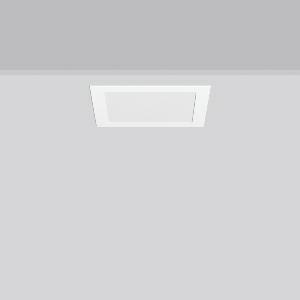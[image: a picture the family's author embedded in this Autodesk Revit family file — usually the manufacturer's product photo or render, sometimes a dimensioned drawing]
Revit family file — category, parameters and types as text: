
# Revit family: toledo_flat_square_e_901487_002_7142
name_source: partatom
category: Lighting Fixtures
units: mm (PartAtom-declared; Revit-internal decimal feet)

## family parameters
Cut with Voids When Loaded = No
Host = Face
Light Source = No
Part Type = Normal
Room Calculation Point = No
Round Connector Dimension = Use Diameter
Shared = No

## types (1)
- TOLEDO FLAT square E (1 x LED Modul 830, 1650 lm, 3000)
    Apparent Load = 17 VA
    CIE Flux Codes = 48 80 96 100 100
    Color Rendering = 80
    Color Temperature = 3000
    Default Elevation = 1800 mm
    Description = Series: TOLEDO FLAT square
Ultra thin recessed downlight. Housing: die-cast aluminium. Light guide and diffuser made of non-yellowing PMMA, opal matt. Ceiling installation with spring system. Mounting depth depends on ceiling strength. Suitable for through-wiring with separately available accessories. Surface mounted housing as accessory for all sizes. Retrofittable decorative cylinders made of chintz fabric as accessory, optional with satin finish plastic diffuser. Through-wiring box (5 pole) available as accessory. 
Colour: white
Length: 225 mm
Width: 225 mm
Height: 3 mm
Cut-out length: 208 mm
Cut-out width: 208 mm
Recess height: 29-56 mm
Luminaire: recess height: 31-51 mm
Lamp: LED
Socket: without socket
Colour temperature: 3000K
Colour rendering index (CRI): 80
System power: 17 W
Rated luminous flux: 1650 lm
Luminous efficiency: 97 lm/W
Control gear: Regulated power supply
Protection class: II
Type of protection: IP 54
    Height = 0 mm  [stored 0 ft]
    Lamp = 1 x LED Modul 830
    Lamp Light Flux = 1650 lm
    Lamp count = 1
    Length = 225 mm
    Lifetime = 50000 h
    Luminous efficacy = 97 lm/W
    Manufacturer = RZB
    ModVariant = No
    Model = 901487.002
    Mounting Place = Ceiling
    Mounting Type = Recessed
    Number of Poles = 1
    OnlyDefault = Yes
    Power Factor = 1
    Product Name = TOLEDO FLAT square E
    Product group = Recessed downlights
    ProductGroupID = 402
    Protection Class = Protection class II
    Protection Degree = IP 20
    RLX_Detail_Level = 1
    RLX_Emergency_Light_Flux = 0 lm
    RLX_Emergency_Type = 0
    RLX_Emergency_Type_DB = No
    RlxData = <blob elided: 58861 chars, md5=ad590975>
    Socket = socket
    Standby Power = 0 W
    System Light Flux = 1650 lm
    System Power = 17 W
    Type Comments = Product without accessories
    Type Image = 901487.002.jpg
    URL = http://relux.com
    VarID = ---
    Voltage = 230 V
    Voltage Range = 220-240 V
    Weight = 0.00 kg
    Width = 225 mm

note: [stored X ft] marks values corroborated as IEEE doubles in the binary element streams (Revit-internal decimal feet)

## geometry (parser evidence)
native form markers: Blend x4, Sweep x10
no freeform markers — native parametric forms only
